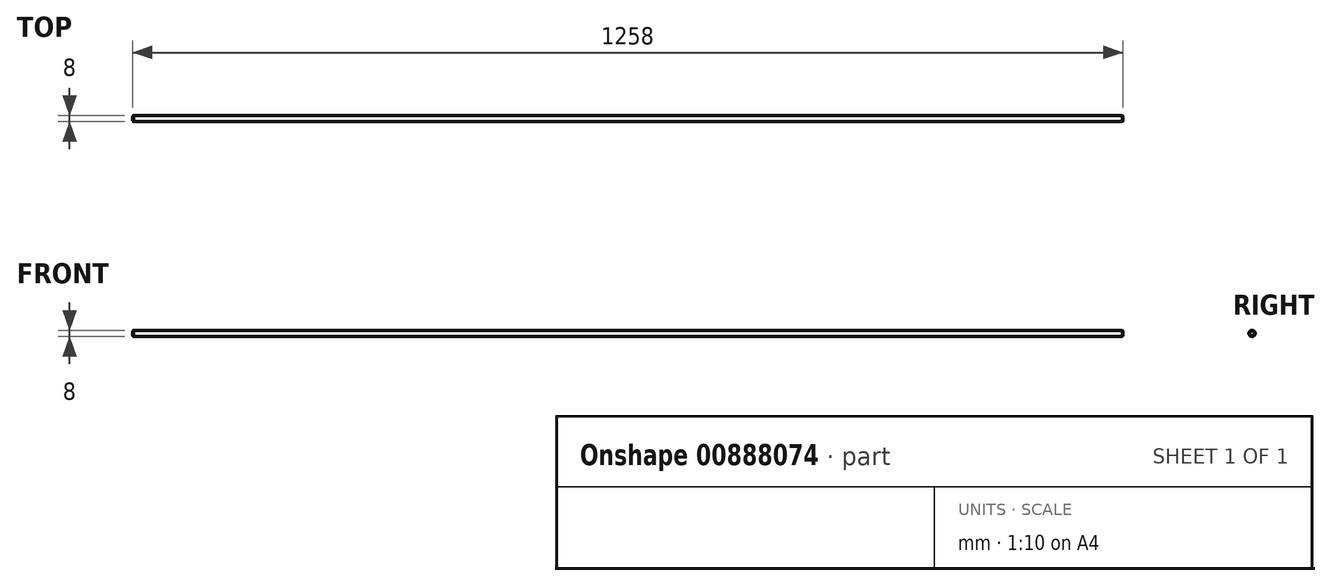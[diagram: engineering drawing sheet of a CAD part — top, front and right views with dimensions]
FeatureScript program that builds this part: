
annotation { "Feature Type Name" : "Feature", "Feature Type Description" : "" }
export const myFeature = defineFeature(function(context is Context, id is Id, definition is map)
    precondition{}
    {
        {
            var Q0;
            Q0=qCreatedBy(makeId("Right.planeOp"),FACE);
            var sketch = newSketch(context, id + "F0", { "sketchPlane" : qUnion([Q0])});
            skCircle(sketch, "E0", {"center": v(0, 0) * mm, "radius": 4 * mm});
            skSolve(sketch);
        }
        {
            var Q0;
            Q0=qSketchRegion(id+"F0",true);
            extrude(context, id + "F1", {"entities" : qUnion([Q0]), "depth" : 1258 * mm, "symmetric" : true});
        }
        {
            var Q0;
            Q0=makeQuery(id+"F1.opExtrude","CAP_EDGE",EDGE,{"disambiguationData":[OSD([sQuery(id+"F0.wireOp",EDGE,"E0")])],"isStart":false});
            var Q1;
            Q1=makeQuery(id+"F1.opExtrude","CAP_EDGE",EDGE,{"disambiguationData":[OSD([sQuery(id+"F0.wireOp",EDGE,"E0")])],"isStart":true});
            chamfer(context, id + "F2", {"entities" : qUnion([Q0, Q1]), "width" : 1 * mm, "tangentPropagation" : true});
        }
    });
